# Revit family: IS_LDV_BD653_BIM_NL
name_source: partatom
category: Plumbing Fixtures
units: mm (PartAtom-declared; Revit-internal decimal feet)

## family parameters
Cut with Voids When Loaded = No
Host = Face
OmniClass Number = 23.45.55.17
OmniClass Title = Mixing Faucets
Part Type = Normal
Room Calculation Point = No
Round Connector Dimension = Use Diameter
Shared = Yes

## types (4) — shared parameters
Afmetingen = 52 x 171 x 178 mm
AfstandsEenheid = Millimeter
AreaUnits = Millimeter
Assembly Code = C1030200
AssetType = Fixed
Auteur = Ideal Standard
BIMobject category = Sanitary: Taps & Mixers
BREEAMApproved = No
Brand = Ideal Standard
Brand url = https://www.idealstandard.nl
ConnectionType = Plumbing
CurrencyUnit = €
CurrentRevision = 1
Date of publishing = 2023-09-29
Default Elevation = 800 mm  [stored 2.62467 ft]
DurationUnit = year
DuurEenheid = Jahr
ECA = No
EPD = https://www.idealstandard.nl
Edition number = 1
ExpectedLife = 30
FaucetFunction = MIXED
FaucetOperation = LEVERHANDLE
FaucetType = PILLAR
FlowRate = 5L/hr @ 3bar
Garantieunits = Jahr
GemaaktOp = 2023-09-29
Help = https://www.idealstandard.nl
Hoogte = 177,829748763169
Hulp = https://www.idealstandard.nl
IFC Classification = Sanitary Terminal
IfcExportAs = IfcValveType
IfcExportType = FAUCET
Installatieinstructies = https://www.idealstandard.nl
InstallationInstructions = https://www.idealstandard.nl
Lengte = 171 mm
LinearUnits = millimeters
Manufacturer = Ideal Standard
Manufacturer name = Ideal Standard
ManufacturerURL = https://www.idealstandard.nl
Materiaal = Messing
Material = Messing
Material main = Messing
Merk = Ideal Standard
NBSReference = 45-35-70/???
Name = BasinMixer_LaDolceVita_BD653_IdealStandard
NettWeight = 1,39 KG
NominalHeight = 178 mm
NominalLength = 171 mm
NominalWidth = 52 mm
OmniClass Code = 23-31 11 00 | Faucets
OmniClass Description = Faucets
Product SKU = BD653
Product data url = https://www.idealstandard.nl
Product family = LaDolceVita
Product url = https://www.idealstandard.nl
ProductInformation = https://www.idealstandard.nl
Productinformatie = https://www.idealstandard.nl
Shape = Cylindical
Size = 52 x 171 x 178 mm
Space = Internal
SpareParts = https://www.idealstandard.nl
TMV3 = Yes
Technical description = https://www.idealstandard.nl
Telefoonnummer = 077 355 08 08
TestPressure = 10 Bar
Typeconnectie = Installation
URL = https://www.idealstandard.de
Uniclass2015Beschrijving = Shower manual water supply sets
Uniclass2015Code = Pr_40_20_87_78
Uniclass2015Description = Shower manual water supply sets
Uniclass2015Title = Shower manual water supply sets
Uniclass2015Version = v1.1
Urlproducent = https://www.idealstandard.de
ValutaEenheid = €
Versie = 1
Version = 1
VolumeUnits = Liter
Volumeunits = Liter
Vorm = Zylindrisch
WRAS = Yes
WarrantyDescription = Manufacturers Warranty
WarrantyDurationParts = 5
WarrantyDurationUnit = year
WarrantyGuarantorParts = https://www.idealstandard.nl
WaterEfficientProduct = No
Wisselstukken = https://www.idealstandard.nl
WorkingPressure = 5 Bar
Youtube clip = https://www.youtube.com
zero-valued in all types: Breedte, BrutoGewicht, CWFU, Cost, Diepte, HWFU, Nettogewicht, Vervangingskosten, WFU

## per-type parameters (varying)
| type | Afwerking | Artikelnummer | Artikelomschrijving | BIMObjectName | BarCode | Barcode | BimObjectNaam | Color | Description | Eigenschappen | Features | Finish | GTIN code | Kleur | MAT | Model | ModelNumber | ModelReference | Product name |
| BD653A2 - LDV BSN MXR R-MTD 5L PUW/M BR GOLD | Gebürstetes Gold | BD653A2 | La Dolce Vita Waschtischmischer Randmontage 5L PUW/M Gebürstetes Gold | IS_IdealStandard_BasinMixer_LaDolceVita_BD653A2 | 3800861127031 | 3800861127031 | IS_IdealStandard_BasinMixer_LaDolceVita_BD653A2 | Brushed Gold | La Dolce Vita  Basin Mixer Rim Mounted 5L PUW/M Brushed Gold | La Dolce Vita Waschtischmischer Randmontage 5L PUW/M Gebürstetes Gold | La Dolce Vita  Basin Mixer Rim Mounted 5L PUW/M Brushed Gold | Brushed Gold | 3800861127031 | Gebürstetes Gold | Brushed Gold-A2 | BD653A2 | BD653A2 | La Dolce Vita  Basin Mixer Rim Mounted 5L PUW/M Brushed Gold | LDV BSN MXR R-MTD 5L PUW/M BR GOLD |
| BD653A5 - LDV BSN MXR R-MTD 5L PUW/M MGNGR | Magnetisches Grau | BD653A5 | La Dolce Vita Waschtischmischer Randmontage 5L PUW/M Magnetgrau | IS_IdealStandard_BasinMixer_LaDolceVita_BD653A5 | 3800861127383 | 3800861127383 | IS_IdealStandard_BasinMixer_LaDolceVita_BD653A5 | Magnetic Grey | La Dolce Vita  Basin Mixer Rim Mounted 5L PUW/M Magnetic Grey | La Dolce Vita Waschtischmischer Randmontage 5L PUW/M Magnetgrau | La Dolce Vita  Basin Mixer Rim Mounted 5L PUW/M Magnetic Grey | Magnetic Grey | 3800861127383 | Magnetisches Grau | Magnetic Grey-A5 | BD653A5 | BD653A5 | La Dolce Vita  Basin Mixer Rim Mounted 5L PUW/M Magnetic Grey | LDV BSN MXR R-MTD 5L PUW/M MGNGR |
| BD653AA - LDV BSN MXR R-MTD 5L PUW/M CHR | Chrom | BD653AA | La Dolce Vita Waschtischmischer Randmontage 5L PUW/M Chrom | IS_IdealStandard_BasinMixer_LaDolceVita_BD653AA | 3800861126676 | 3800861126676 | IS_IdealStandard_BasinMixer_LaDolceVita_BD653AA | Chrome | La Dolce Vita  Basin Mixer Rim Mounted 5L PUW/M Chrome | La Dolce Vita Waschtischmischer Randmontage 5L PUW/M Chrom | La Dolce Vita  Basin Mixer Rim Mounted 5L PUW/M Chrome | Chrome | 3800861126676 | Chrom | Chrome-AA | BD653AA | BD653AA | La Dolce Vita  Basin Mixer Rim Mounted 5L PUW/M Chrome | LDV BSN MXR R-MTD 5L PUW/M CHR |
| BD653GN - LDV BSN MXR R-MTD 5L PUW/M SILV ST | Silberner Sturm | BD653GN | La Dolce Vita Waschtischmischer Randmontage 5L PUW/M Silbersturm | IS_IdealStandard_BasinMixer_LaDolceVita_BD653GN | 3800861127734 | 3800861127734 | IS_IdealStandard_BasinMixer_LaDolceVita_BD653GN | Silver storm | La Dolce Vita  Basin Mixer Rim Mounted 5L PUW/M Silver Storm | La Dolce Vita Waschtischmischer Randmontage 5L PUW/M Silbersturm | La Dolce Vita  Basin Mixer Rim Mounted 5L PUW/M Silver Storm | Silver storm | 3800861127734 | Silberner Sturm | Silver Storm-GN | BD653GN | BD653GN | La Dolce Vita  Basin Mixer Rim Mounted 5L PUW/M Silver Storm | LDV BSN MXR R-MTD 5L PUW/M SILV ST |

note: [stored X ft] marks values corroborated as IEEE doubles in the binary element streams (Revit-internal decimal feet)

## geometry (parser evidence)
native form markers: Blend x2, Sweep x3
no freeform markers — native parametric forms only
